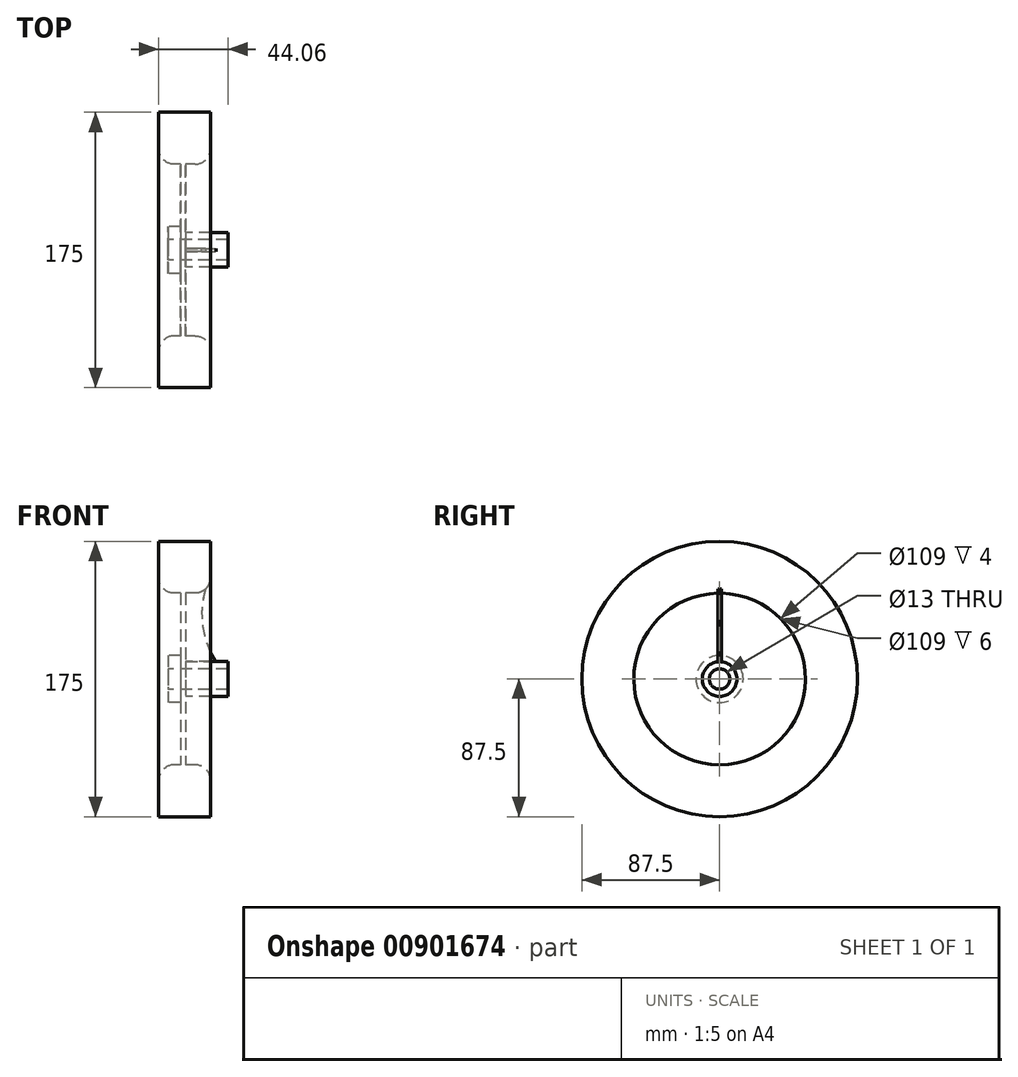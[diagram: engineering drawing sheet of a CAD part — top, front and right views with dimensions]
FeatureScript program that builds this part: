
annotation { "Feature Type Name" : "Feature", "Feature Type Description" : "" }
export const myFeature = defineFeature(function(context is Context, id is Id, definition is map)
    precondition{}
    {
        {
            var Q0;
            Q0=qCreatedBy(makeId("Top.planeOp"),FACE);
            var sketch = newSketch(context, id + "F0", { "sketchPlane" : qUnion([Q0])});
            skLineSegment(sketch, "E0", {"start": v(-69.33, 0) * mm, "end": v(65.9, 0) * mm, "construction": true});
            skSolve(sketch);
        }
        {
            var Q0;
            Q0=qCreatedBy(makeId("Front.planeOp"),FACE);
            var sketch = newSketch(context, id + "F1", { "sketchPlane" : qUnion([Q0])});
            skLineSegment(sketch, "E1", {"start": v(17.94, 87.5) * mm, "end": v(17.94, 54.5) * mm});
            skLineSegment(sketch, "E2", {"start": v(17.94, 54.5) * mm, "end": v(1.94, 54.5) * mm});
            skLineSegment(sketch, "E3", {"start": v(1.94, 54.5) * mm, "end": v(1.94, 11) * mm});
            skLineSegment(sketch, "E4", {"start": v(1.94, 11) * mm, "end": v(29, 11) * mm});
            skLineSegment(sketch, "E5", {"start": v(29, 11) * mm, "end": v(29, 6.5) * mm});
            skLineSegment(sketch, "E6", {"start": v(29, 6.5) * mm, "end": v(-9, 6.5) * mm});
            skLineSegment(sketch, "E7", {"start": v(-9, 6.5) * mm, "end": v(-9, 15) * mm});
            skLineSegment(sketch, "E8", {"start": v(-9, 15) * mm, "end": v(-1.06, 15) * mm});
            skLineSegment(sketch, "E9", {"start": v(17.94, 87.5) * mm, "end": v(-15.06, 87.5) * mm});
            skLineSegment(sketch, "E10", {"start": v(-15.06, 87.5) * mm, "end": v(-15.06, 54.5) * mm});
            skLineSegment(sketch, "E11", {"start": v(-15.06, 54.5) * mm, "end": v(-1.06, 54.5) * mm});
            skLineSegment(sketch, "E12", {"start": v(-1.06, 54.5) * mm, "end": v(-1.06, 15) * mm});
            skSolve(sketch);
        }
        {
            var Q0;
            Q0=makeQuery(id+"F1.imprint","IMPRINT",FACE,{"disambiguationData":[TD([[makeQuery(id+"F1.imprint","IMPRINT",EDGE,{"derivedFrom":sQuery(id+"F1.wireOp",EDGE,"E1")}),-1.0]])]});
            var Q1;
            Q1=sQuery(id+"F0.wireOp",EDGE,"E0");
            revolve(context, id + "F2", {"surfaceOperationType" : NewSurfaceOperationType.NEW, "entities" : qUnion([Q0]), "axis" : qUnion([Q1]), "revolveType" : RevolveType.FULL});
        }
        {
            var Q0;
            Q0=makeQuery(id+"F2.opRevolve","SWEPT_EDGE",EDGE,{"disambiguationData":[OSD([sQuery(id+"F1.wireOp",EDGE,"E1"),sQuery(id+"F1.wireOp",EDGE,"E2")])]});
            var Q1;
            Q1=makeQuery(id+"F2.opRevolve","SWEPT_EDGE",EDGE,{"disambiguationData":[OSD([sQuery(id+"F1.wireOp",EDGE,"E10"),sQuery(id+"F1.wireOp",EDGE,"E11")])]});
            fillet(context, id + "F3", {"entities" : qUnion([Q0, Q1]), "radius" : 10 * mm, "tangentPropagation" : true, "allowEdgeOverflow" : false});
        }
        {
            var Q0;
            Q0=qCreatedBy(makeId("Front.planeOp"),FACE);
            var sketch = newSketch(context, id + "F4", { "sketchPlane" : qUnion([Q0])});
            skArc(sketch, "E13", {"start": v(14.64, 57.1) * mm, "mid": v(12.87, 33.39) * mm, "end": v(21.26, 11.15) * mm});
            skLineSegment(sketch, "E14", {"start": v(14.64, 57.1) * mm, "end": v(2.09, 57.1) * mm});
            skLineSegment(sketch, "E15", {"start": v(2.09, 57.1) * mm, "end": v(2.09, 11.04) * mm});
            skLineSegment(sketch, "E16", {"start": v(2.09, 11.04) * mm, "end": v(21.26, 11.15) * mm});
            skSolve(sketch);
        }
        {
            var Q0;
            Q0=qSketchRegion(id+"F4",true);
            extrude(context, id + "F5", {"entities" : qUnion([Q0]), "operationType" : NewBodyOperationType.ADD, "endBound" : BoundingType.SYMMETRIC, "depth" : 2 * mm, "offsetDistance" : 25.4 * mm});
        }
    });
